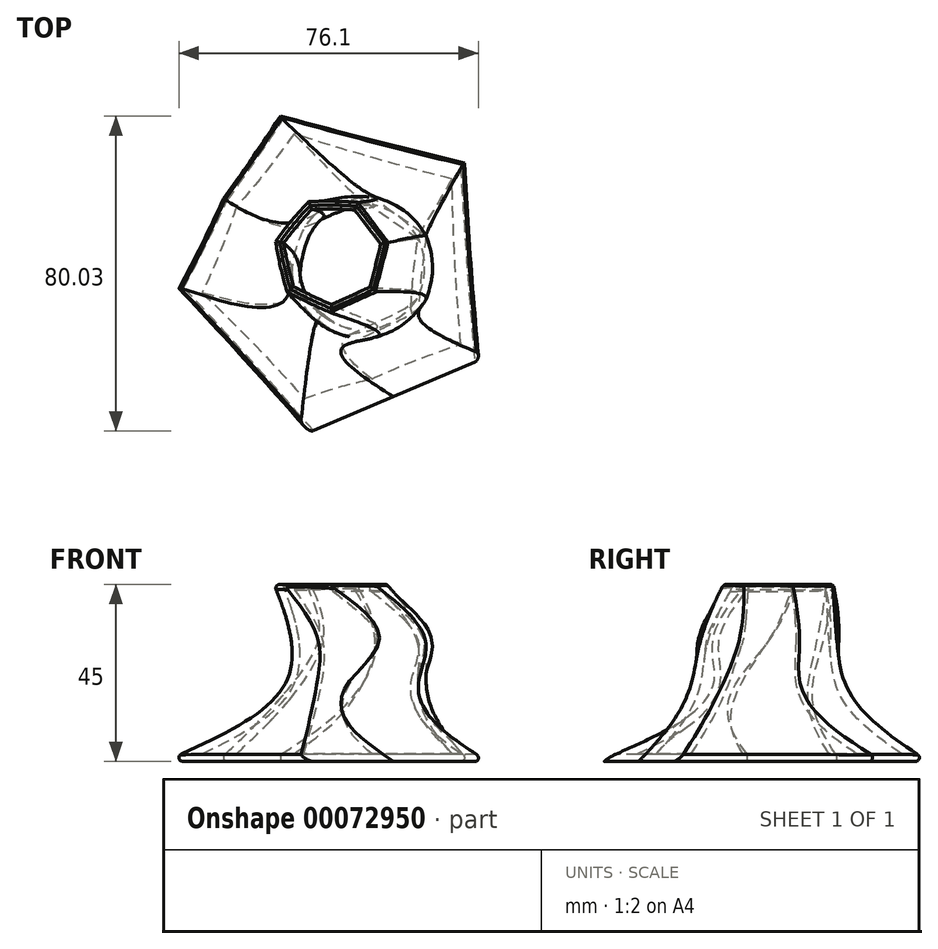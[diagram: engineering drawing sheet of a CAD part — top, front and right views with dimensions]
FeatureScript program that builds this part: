
annotation { "Feature Type Name" : "Feature", "Feature Type Description" : "" }
export const myFeature = defineFeature(function(context is Context, id is Id, definition is map)
    precondition{}
    {
        {
            var Q0;
            Q0=qCreatedBy(makeId("Top.planeOp"),FACE);
            var sketch = newSketch(context, id + "F0", { "sketchPlane" : qUnion([Q0])});
            skCircle(sketch, "E0.cCircle", {"center": v(0, 0) * mm, "radius": 35.78 * mm, "construction": true});
            skLineSegment(sketch, "E0.0", {"start": v(33.33, 29.06) * mm, "end": v(37.94, -22.72) * mm});
            skLineSegment(sketch, "E0.1", {"start": v(37.94, -22.72) * mm, "end": v(-9.88, -43.1) * mm});
            skLineSegment(sketch, "E0.2", {"start": v(-9.88, -43.1) * mm, "end": v(-44.05, -3.92) * mm});
            skLineSegment(sketch, "E0.3", {"start": v(-44.05, -3.92) * mm, "end": v(-17.34, 40.68) * mm});
            skLineSegment(sketch, "E0.4", {"start": v(-17.34, 40.68) * mm, "end": v(33.33, 29.06) * mm});
            skPoint(sketch, "E0.0.midPoint", {"position": v(35.64, 3.17) * mm});
            skSolve(sketch);
        }
        {
            var Q0;
            Q0=qCreatedBy(makeId("Top.planeOp"),FACE);
            cPlane(context, id + "F1", {"entities" : qUnion([Q0]), "cplaneType" : CPlaneType.OFFSET, "offset" : 20 * mm, "width" : 150 * mm, "height" : 150 * mm});
        }
        {
            var Q0;
            Q0=qCreatedBy(id+"F1.planeOp",FACE);
            var sketch = newSketch(context, id + "F2", { "sketchPlane" : qUnion([Q0])});
            skCircle(sketch, "E1.cCircle", {"center": v(4.52, 0) * mm, "radius": 16.96 * mm, "construction": true});
            skLineSegment(sketch, "E1.0", {"start": v(22.34, 8.1) * mm, "end": v(20.45, -11.39) * mm});
            skLineSegment(sketch, "E1.1", {"start": v(20.45, -11.39) * mm, "end": v(2.62, -19.49) * mm});
            skLineSegment(sketch, "E1.2", {"start": v(2.62, -19.49) * mm, "end": v(-13.3, -8.1) * mm});
            skLineSegment(sketch, "E1.3", {"start": v(-13.3, -8.1) * mm, "end": v(-11.4, 11.39) * mm});
            skLineSegment(sketch, "E1.4", {"start": v(-11.4, 11.39) * mm, "end": v(6.42, 19.49) * mm});
            skLineSegment(sketch, "E1.5", {"start": v(6.42, 19.49) * mm, "end": v(22.34, 8.1) * mm});
            skPoint(sketch, "E1.0.midPoint", {"position": v(21.4, -1.64) * mm});
            skSolve(sketch);
        }
        {
            var Q0;
            Q0=qCreatedBy(makeId("Top.planeOp"),FACE);
            cPlane(context, id + "F3", {"entities" : qUnion([Q0]), "cplaneType" : CPlaneType.OFFSET, "offset" : 30 * mm, "width" : 150 * mm, "height" : 150 * mm});
        }
        {
            var Q0;
            Q0=qCreatedBy(id+"F3.planeOp",FACE);
            var sketch = newSketch(context, id + "F4", { "sketchPlane" : qUnion([Q0])});
            skCircle(sketch, "E2", {"center": v(6.08, 0) * mm, "radius": 17.9 * mm});
            skSolve(sketch);
        }
        {
            var Q0;
            Q0=qCreatedBy(makeId("Top.planeOp"),FACE);
            cPlane(context, id + "F5", {"entities" : qUnion([Q0]), "cplaneType" : CPlaneType.OFFSET, "offset" : 45 * mm, "width" : 150 * mm, "height" : 150 * mm});
        }
        {
            var Q0;
            Q0=qCreatedBy(id+"F5.planeOp",FACE);
            var sketch = newSketch(context, id + "F6", { "sketchPlane" : qUnion([Q0])});
            skCircle(sketch, "E3.cCircle", {"center": v(-2.05, 3.32) * mm, "radius": 13.27 * mm, "construction": true});
            skLineSegment(sketch, "E3.0", {"start": v(12.4, 6.19) * mm, "end": v(9.2, -6.19) * mm});
            skLineSegment(sketch, "E3.1", {"start": v(9.2, -6.19) * mm, "end": v(-2.47, -11.4) * mm});
            skLineSegment(sketch, "E3.2", {"start": v(-2.47, -11.4) * mm, "end": v(-13.83, -5.53) * mm});
            skLineSegment(sketch, "E3.3", {"start": v(-13.83, -5.53) * mm, "end": v(-16.31, 7) * mm});
            skLineSegment(sketch, "E3.4", {"start": v(-16.31, 7) * mm, "end": v(-8.06, 16.77) * mm});
            skLineSegment(sketch, "E3.5", {"start": v(-8.06, 16.77) * mm, "end": v(4.71, 16.4) * mm});
            skLineSegment(sketch, "E3.6", {"start": v(4.71, 16.4) * mm, "end": v(12.4, 6.19) * mm});
            skPoint(sketch, "E3.0.midPoint", {"position": v(10.8, 0) * mm});
            skSolve(sketch);
        }
        {
            var Q0;
            Q0=qSketchRegion(id+"F0",true);
            var Q1;
            Q1=qSketchRegion(id+"F2",true);
            var Q2;
            Q2=qSketchRegion(id+"F4",true);
            var Q3;
            Q3=makeQuery(id+"F6.imprint","IMPRINT",FACE,{"disambiguationData":[TD([[makeQuery(id+"F6.imprint","IMPRINT",EDGE,{"derivedFrom":sQuery(id+"F6.wireOp",EDGE,"E3.0")}),-1.0]])]});
            loft(context, id + "F7", {"sheetProfilesArray" : [{ "sheetProfileEntities" : qUnion([Q0]) }, { "sheetProfileEntities" : qUnion([Q1]) }, { "sheetProfileEntities" : qUnion([Q2]) }, { "sheetProfileEntities" : qUnion([Q3]) }]});
        }
        {
            var Q0;
            Q0=makeQuery(id+"F7.opLoft","CAP_FACE",FACE,{"disambiguationData":[OSD([makeQuery(id+"F6.imprint","IMPRINT",FACE,{"disambiguationData":[TD([[makeQuery(id+"F6.imprint","IMPRINT",EDGE,{"derivedFrom":sQuery(id+"F6.wireOp",EDGE,"E3.0")}),-1.0]])]})])],"isStart":true});
            shell(context, id + "F8", {"entities" : qUnion([Q0]), "thickness" : 2 * mm});
        }
        {
            var Q0;
            Q0=makeQuery(id+"F7.opLoft","MID_CAP_EDGE",EDGE,{"disambiguationData":[OSD([sQuery(id+"F0.wireOp",EDGE,"E0.2"),sQuery(id+"F0.wireOp",EDGE,"E0.3"),sQuery(id+"F0.wireOp",EDGE,"E0.4")])],"capPos":0.0});
            var Q1;
            Q1=makeQuery(id+"F7.opLoft","MID_CAP_EDGE",EDGE,{"disambiguationData":[OSD([sQuery(id+"F0.wireOp",EDGE,"E0.1"),sQuery(id+"F0.wireOp",EDGE,"E0.2"),sQuery(id+"F0.wireOp",EDGE,"E0.3")])],"capPos":0.0});
            var Q2;
            Q2=makeQuery(id+"F7.opLoft","MID_CAP_EDGE",EDGE,{"disambiguationData":[OSD([sQuery(id+"F0.wireOp",EDGE,"E0.0"),sQuery(id+"F0.wireOp",EDGE,"E0.1"),sQuery(id+"F0.wireOp",EDGE,"E0.2")])],"capPos":0.0});
            var Q3;
            Q3=makeQuery(id+"F7.opLoft","MID_CAP_EDGE",EDGE,{"disambiguationData":[OSD([sQuery(id+"F0.wireOp",EDGE,"E0.0"),sQuery(id+"F0.wireOp",EDGE,"E0.1"),sQuery(id+"F0.wireOp",EDGE,"E0.4")])],"capPos":0.0});
            var Q4;
            Q4=makeQuery(id+"F7.opLoft","MID_CAP_EDGE",EDGE,{"disambiguationData":[OSD([sQuery(id+"F0.wireOp",EDGE,"E0.4"),sQuery(id+"F6.wireOp",EDGE,"E3.0"),sQuery(id+"F6.wireOp",EDGE,"E3.5"),sQuery(id+"F6.wireOp",EDGE,"E3.6")])],"capPos":0.0});
            var Q5;
            Q5=makeQuery(id+"F7.opLoft","MID_CAP_EDGE",EDGE,{"disambiguationData":[OSD([sQuery(id+"F0.wireOp",EDGE,"E0.3"),sQuery(id+"F0.wireOp",EDGE,"E0.4"),sQuery(id+"F6.wireOp",EDGE,"E3.5"),sQuery(id+"F6.wireOp",EDGE,"E3.6")])],"capPos":0.0});
            var Q6;
            Q6=makeQuery(id+"F7.opLoft","MID_CAP_EDGE",EDGE,{"disambiguationData":[OSD([sQuery(id+"F6.wireOp",EDGE,"E3.2"),sQuery(id+"F6.wireOp",EDGE,"E3.3"),sQuery(id+"F6.wireOp",EDGE,"E3.4")])],"capPos":3.0});
            var Q7;
            Q7=makeQuery(id+"F7.opLoft","MID_CAP_EDGE",EDGE,{"disambiguationData":[OSD([sQuery(id+"F6.wireOp",EDGE,"E3.1"),sQuery(id+"F6.wireOp",EDGE,"E3.2"),sQuery(id+"F6.wireOp",EDGE,"E3.3")])],"capPos":3.0});
            var Q8;
            Q8=makeQuery(id+"F7.opLoft","MID_CAP_EDGE",EDGE,{"disambiguationData":[OSD([sQuery(id+"F6.wireOp",EDGE,"E3.0"),sQuery(id+"F6.wireOp",EDGE,"E3.1"),sQuery(id+"F6.wireOp",EDGE,"E3.2")])],"capPos":3.0});
            var Q9;
            Q9=makeQuery(id+"F7.opLoft","MID_CAP_EDGE",EDGE,{"disambiguationData":[OSD([sQuery(id+"F6.wireOp",EDGE,"E3.0"),sQuery(id+"F6.wireOp",EDGE,"E3.1"),sQuery(id+"F6.wireOp",EDGE,"E3.6")])],"capPos":3.0});
            var Q10;
            Q10=makeQuery(id+"F7.opLoft","MID_CAP_EDGE",EDGE,{"disambiguationData":[OSD([sQuery(id+"F6.wireOp",EDGE,"E3.0"),sQuery(id+"F6.wireOp",EDGE,"E3.5"),sQuery(id+"F6.wireOp",EDGE,"E3.6")])],"capPos":3.0});
            var Q11;
            Q11=makeQuery(id+"F7.opLoft","MID_CAP_EDGE",EDGE,{"disambiguationData":[OSD([sQuery(id+"F6.wireOp",EDGE,"E3.4"),sQuery(id+"F6.wireOp",EDGE,"E3.5"),sQuery(id+"F6.wireOp",EDGE,"E3.6")])],"capPos":3.0});
            var Q12;
            Q12=makeQuery(id+"F7.opLoft","MID_CAP_EDGE",EDGE,{"disambiguationData":[OSD([sQuery(id+"F6.wireOp",EDGE,"E3.3"),sQuery(id+"F6.wireOp",EDGE,"E3.4"),sQuery(id+"F6.wireOp",EDGE,"E3.5")])],"capPos":3.0});
            var Q13;
            Q13=makeQuery(id+"F8.opShell","OFFSET_EDGE",EDGE,{"disambiguationData":[OSD([sQuery(id+"F6.wireOp",EDGE,"E3.3"),sQuery(id+"F6.wireOp",EDGE,"E3.4"),sQuery(id+"F6.wireOp",EDGE,"E3.5")])]});
            var Q14;
            Q14=makeQuery(id+"F8.opShell","OFFSET_EDGE",EDGE,{"disambiguationData":[OSD([sQuery(id+"F6.wireOp",EDGE,"E3.2"),sQuery(id+"F6.wireOp",EDGE,"E3.3"),sQuery(id+"F6.wireOp",EDGE,"E3.4")])]});
            var Q15;
            Q15=makeQuery(id+"F8.opShell","OFFSET_EDGE",EDGE,{"disambiguationData":[OSD([sQuery(id+"F6.wireOp",EDGE,"E3.1"),sQuery(id+"F6.wireOp",EDGE,"E3.2"),sQuery(id+"F6.wireOp",EDGE,"E3.3")])]});
            var Q16;
            Q16=makeQuery(id+"F8.opShell","OFFSET_EDGE",EDGE,{"disambiguationData":[OSD([sQuery(id+"F6.wireOp",EDGE,"E3.0"),sQuery(id+"F6.wireOp",EDGE,"E3.1"),sQuery(id+"F6.wireOp",EDGE,"E3.2")])]});
            var Q17;
            Q17=makeQuery(id+"F8.opShell","OFFSET_EDGE",EDGE,{"disambiguationData":[OSD([sQuery(id+"F6.wireOp",EDGE,"E3.0"),sQuery(id+"F6.wireOp",EDGE,"E3.1"),sQuery(id+"F6.wireOp",EDGE,"E3.6")])]});
            var Q18;
            Q18=makeQuery(id+"F8.opShell","OFFSET_EDGE",EDGE,{"disambiguationData":[OSD([sQuery(id+"F6.wireOp",EDGE,"E3.0"),sQuery(id+"F6.wireOp",EDGE,"E3.5"),sQuery(id+"F6.wireOp",EDGE,"E3.6")])]});
            var Q19;
            Q19=makeQuery(id+"F8.opShell","OFFSET_EDGE",EDGE,{"disambiguationData":[OSD([sQuery(id+"F6.wireOp",EDGE,"E3.4"),sQuery(id+"F6.wireOp",EDGE,"E3.5"),sQuery(id+"F6.wireOp",EDGE,"E3.6")])]});
            fillet(context, id + "F9", {"entities" : qUnion([Q0, Q1, Q2, Q3, Q4, Q5, Q6, Q7, Q8, Q9, Q10, Q11, Q12, Q13, Q14, Q15, Q16, Q17, Q18, Q19]), "radius" : 1 * mm, "tangentPropagation" : true, "allowEdgeOverflow" : false});
        }
    });
